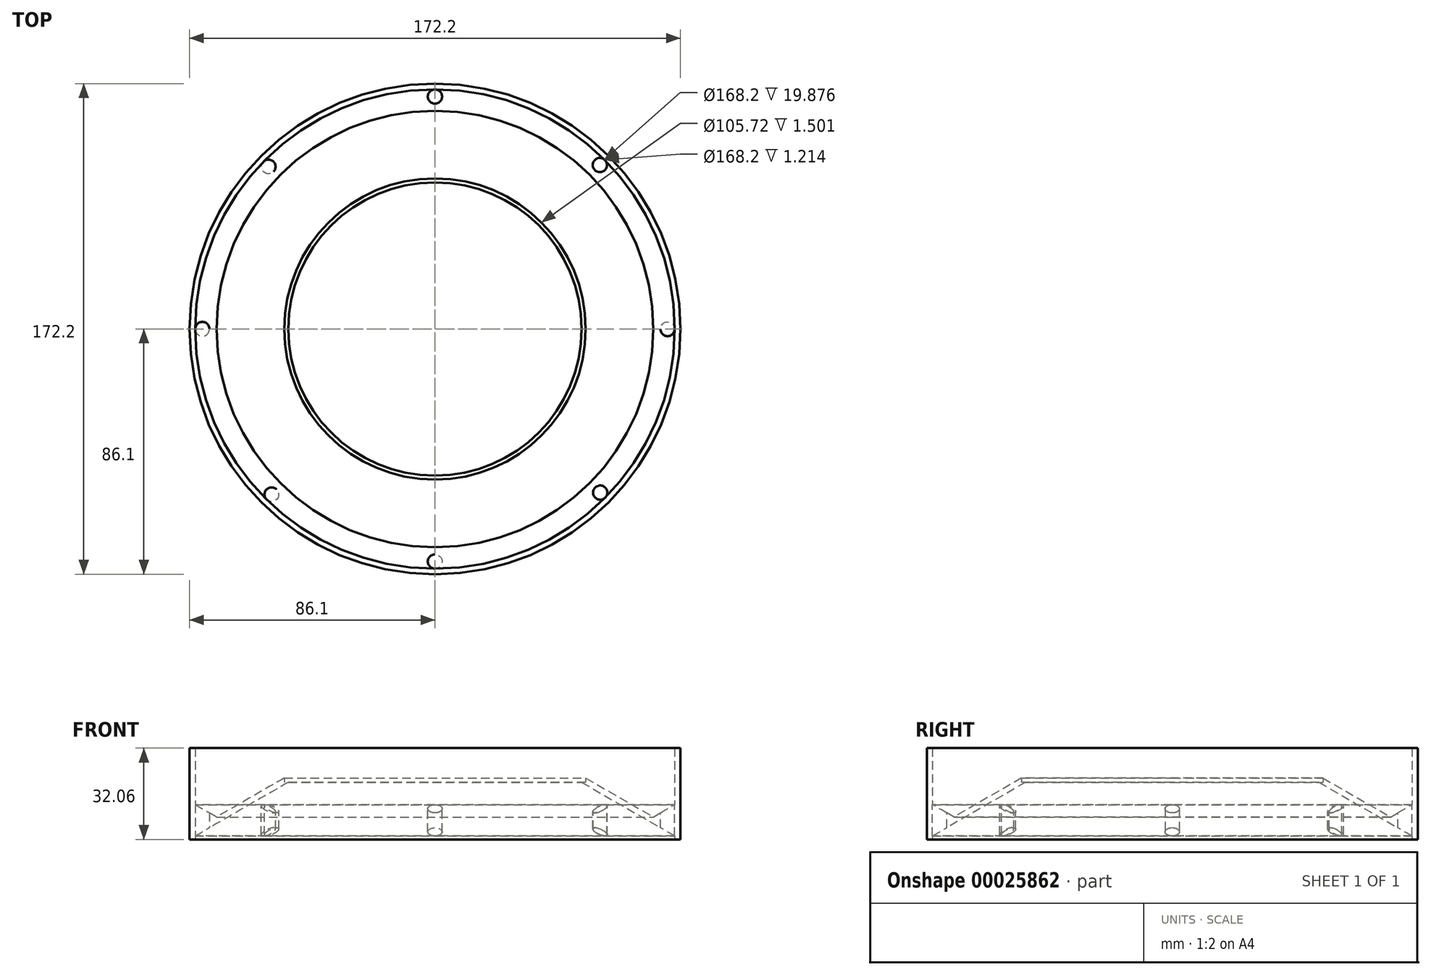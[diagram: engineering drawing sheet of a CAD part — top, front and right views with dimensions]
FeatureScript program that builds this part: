
annotation { "Feature Type Name" : "Feature", "Feature Type Description" : "" }
export const myFeature = defineFeature(function(context is Context, id is Id, definition is map)
    precondition{}
    {
        {
            var Q0;
            Q0=qCreatedBy(makeId("Top.planeOp"),FACE);
            var sketch = newSketch(context, id + "F0", { "sketchPlane" : qUnion([Q0])});
            skCircle(sketch, "E0", {"center": v(0, 0) * mm, "radius": 52.86 * mm});
            skSolve(sketch);
        }
        {
            var Q0;
            Q0=qCreatedBy(makeId("Front.planeOp"),FACE);
            var sketch = newSketch(context, id + "F1", { "sketchPlane" : qUnion([Q0])});
            skLineSegment(sketch, "E1", {"start": v(0, -28.34) * mm, "end": v(0, 33.36) * mm});
            skSolve(sketch);
        }
        {
            var Q0;
            Q0=qCreatedBy(makeId("Front.planeOp"),FACE);
            var sketch = newSketch(context, id + "F2", { "sketchPlane" : qUnion([Q0])});
            skLineSegment(sketch, "E2", {"start": v(0, 0) * mm, "end": v(-51.46, 0) * mm});
            skLineSegment(sketch, "E3", {"start": v(-51.46, 0) * mm, "end": v(-86.1, -20) * mm});
            skLineSegment(sketch, "E4", {"start": v(-86.1, -20) * mm, "end": v(-86.1, 12) * mm});
            skLineSegment(sketch, "E5", {"start": v(-86.1, 12) * mm, "end": v(-84.1, 12) * mm});
            skLineSegment(sketch, "E6", {"start": v(-84.1, 12) * mm, "end": v(-84.1, -16.54) * mm});
            skLineSegment(sketch, "E7", {"start": v(-84.1, -16.54) * mm, "end": v(-52, 2) * mm});
            skLineSegment(sketch, "E8", {"start": v(-52, 2) * mm, "end": v(0, 2) * mm});
            skLineSegment(sketch, "E9", {"start": v(0, 2) * mm, "end": v(0, 0) * mm});
            skSolve(sketch);
        }
        {
            var Q0;
            Q0 = qSketchRegion(id + "F2", true);
            var Q1;
            Q1=sQuery(id+"F1.wireOp",EDGE,"E1");
            revolve(context, id + "F3", {"entities" : qUnion([Q0]), "axis" : qUnion([Q1]), "revolveType" : RevolveType.FULL});
        }
        {
            var Q0;
            Q0 = qSketchRegion(id + "F0", true);
            extrude(context, id + "F4", {"entities" : qUnion([Q0]), "operationType" : NewBodyOperationType.REMOVE, "depth" : 9.85 * mm});
        }
        {
            var Q0;
            Q0=qCreatedBy(makeId("Top.planeOp"),FACE);
            var sketch = newSketch(context, id + "F5", { "sketchPlane" : qUnion([Q0])});
            skCircle(sketch, "E10", {"center": v(-81.6, 0) * mm, "radius": 2.5 * mm});
            skCircle(sketch, "E11", {"center": v(0, 0) * mm, "radius": 2.5 * mm});
            skSolve(sketch);
        }
        {
            var Q0;
            Q0 = qSketchRegion(id + "F5", true);
            extrude(context, id + "F6", {"entities" : qUnion([Q0]), "operationType" : NewBodyOperationType.REMOVE, "depth" : 25 * mm, "hasSecondDirection" : true, "secondDirectionOppositeDirection" : true, "secondDirectionDepth" : 25 * mm});
        }
        {
            var Q0;
            Q0=qCreatedBy(makeId("Top.planeOp"),FACE);
            var sketch = newSketch(context, id + "F7", { "sketchPlane" : qUnion([Q0])});
            skCircle(sketch, "E12", {"center": v(-58.42, 56.97) * mm, "radius": 2.5 * mm});
            skCircle(sketch, "E13", {"center": v(0, 81.6) * mm, "radius": 2.5 * mm});
            skCircle(sketch, "E14", {"center": v(57.85, 57.55) * mm, "radius": 2.5 * mm});
            skCircle(sketch, "E15", {"center": v(81.6, 0) * mm, "radius": 2.5 * mm});
            skCircle(sketch, "E16", {"center": v(57.97, -57.43) * mm, "radius": 2.5 * mm});
            skCircle(sketch, "E17", {"center": v(0, -81.6) * mm, "radius": 2.5 * mm});
            skCircle(sketch, "E18", {"center": v(-57.31, -58.09) * mm, "radius": 2.5 * mm});
            skSolve(sketch);
        }
        {
            var Q0;
            Q0 = qSketchRegion(id + "F7", true);
            extrude(context, id + "F8", {"entities" : qUnion([Q0]), "operationType" : NewBodyOperationType.REMOVE, "oppositeDirection" : true, "depth" : 25 * mm, "hasSecondDirection" : true, "secondDirectionOppositeDirection" : false, "secondDirectionDepth" : 25 * mm});
        }
        {
            var Q0;
            Q0=qCreatedBy(makeId("Front.planeOp"),FACE);
            var sketch = newSketch(context, id + "F9", { "sketchPlane" : qUnion([Q0])});
            skLineSegment(sketch, "E19.bottom", {"start": v(-86.1, -20.06) * mm, "end": v(-84.1, -20.06) * mm});
            skLineSegment(sketch, "E19.top", {"start": v(-86.1, -16.32) * mm, "end": v(-84.1, -16.32) * mm});
            skLineSegment(sketch, "E19.left", {"start": v(-86.1, -20.06) * mm, "end": v(-86.1, -16.32) * mm});
            skLineSegment(sketch, "E19.right", {"start": v(-84.1, -20.06) * mm, "end": v(-84.1, -16.32) * mm});
            skSolve(sketch);
        }
        {
            var Q0;
            Q0 = qSketchRegion(id + "F9", true);
            var Q1;
            Q1=sQuery(id+"F1.wireOp",EDGE,"E1");
            revolve(context, id + "F10", {"operationType" : NewBodyOperationType.ADD, "entities" : qUnion([Q0]), "axis" : qUnion([Q1]), "revolveType" : RevolveType.FULL});
        }
        {
            var Q0;
            {var subQ0=sQuery(id+"F2.wireOp",EDGE,"E6");var subQ1=sQuery(id+"F2.wireOp",EDGE,"E7");Q0=makeQuery(id+"F8.boolean.opBoolean","SPLIT",EDGE,{"disambiguationData":[TD([makeQuery(id+"F3.opRevolve","SWEPT_FACE",FACE,{"disambiguationData":[OSD([subQ0])]}),makeQuery(id+"F3.opRevolve","SWEPT_FACE",FACE,{"disambiguationData":[OSD([subQ1])]}),makeQuery(id+"F6.boolean.opBoolean","COPY",FACE,{"derivedFrom":makeQuery(id+"F6.opExtrude","SWEPT_FACE",FACE,{"disambiguationData":[OSD([sQuery(id+"F5.wireOp",EDGE,"E10")])]})}),makeQuery(id+"F8.opExtrude","SWEPT_FACE",FACE,{"disambiguationData":[OSD([sQuery(id+"F7.wireOp",EDGE,"E12")])]})])],"derivedFrom":makeQuery(id+"F3.opRevolve","SWEPT_EDGE",EDGE,{"disambiguationData":[OSD([subQ0,subQ1])]})});}
            var Q1;
            {var subQ0=sQuery(id+"F2.wireOp",EDGE,"E6");var subQ1=sQuery(id+"F2.wireOp",EDGE,"E7");Q1=makeQuery(id+"F8.boolean.opBoolean","SPLIT",EDGE,{"disambiguationData":[TD([makeQuery(id+"F3.opRevolve","SWEPT_FACE",FACE,{"disambiguationData":[OSD([subQ0])]}),makeQuery(id+"F3.opRevolve","SWEPT_FACE",FACE,{"disambiguationData":[OSD([subQ1])]}),makeQuery(id+"F8.opExtrude","SWEPT_FACE",FACE,{"disambiguationData":[OSD([sQuery(id+"F7.wireOp",EDGE,"E12")])]}),makeQuery(id+"F8.opExtrude","SWEPT_FACE",FACE,{"disambiguationData":[OSD([sQuery(id+"F7.wireOp",EDGE,"E13")])]})])],"derivedFrom":makeQuery(id+"F3.opRevolve","SWEPT_EDGE",EDGE,{"disambiguationData":[OSD([subQ0,subQ1])]})});}
            var Q2;
            {var subQ0=sQuery(id+"F2.wireOp",EDGE,"E6");var subQ1=sQuery(id+"F2.wireOp",EDGE,"E7");Q2=makeQuery(id+"F8.boolean.opBoolean","SPLIT",EDGE,{"disambiguationData":[TD([makeQuery(id+"F3.opRevolve","SWEPT_FACE",FACE,{"disambiguationData":[OSD([subQ0])]}),makeQuery(id+"F3.opRevolve","SWEPT_FACE",FACE,{"disambiguationData":[OSD([subQ1])]}),makeQuery(id+"F6.boolean.opBoolean","COPY",FACE,{"derivedFrom":makeQuery(id+"F6.opExtrude","SWEPT_FACE",FACE,{"disambiguationData":[OSD([sQuery(id+"F5.wireOp",EDGE,"E10")])]})}),makeQuery(id+"F8.opExtrude","SWEPT_FACE",FACE,{"disambiguationData":[OSD([sQuery(id+"F7.wireOp",EDGE,"E18")])]})])],"derivedFrom":makeQuery(id+"F3.opRevolve","SWEPT_EDGE",EDGE,{"disambiguationData":[OSD([subQ0,subQ1])]})});}
            var Q3;
            {var subQ0=sQuery(id+"F2.wireOp",EDGE,"E6");var subQ1=sQuery(id+"F2.wireOp",EDGE,"E7");Q3=makeQuery(id+"F8.boolean.opBoolean","SPLIT",EDGE,{"disambiguationData":[TD([makeQuery(id+"F3.opRevolve","SWEPT_FACE",FACE,{"disambiguationData":[OSD([subQ0])]}),makeQuery(id+"F3.opRevolve","SWEPT_FACE",FACE,{"disambiguationData":[OSD([subQ1])]}),makeQuery(id+"F8.opExtrude","SWEPT_FACE",FACE,{"disambiguationData":[OSD([sQuery(id+"F7.wireOp",EDGE,"E17")])]}),makeQuery(id+"F8.opExtrude","SWEPT_FACE",FACE,{"disambiguationData":[OSD([sQuery(id+"F7.wireOp",EDGE,"E18")])]})])],"derivedFrom":makeQuery(id+"F3.opRevolve","SWEPT_EDGE",EDGE,{"disambiguationData":[OSD([subQ0,subQ1])]})});}
            var Q4;
            {var subQ0=sQuery(id+"F2.wireOp",EDGE,"E6");var subQ1=sQuery(id+"F2.wireOp",EDGE,"E7");Q4=makeQuery(id+"F8.boolean.opBoolean","SPLIT",EDGE,{"disambiguationData":[TD([makeQuery(id+"F3.opRevolve","SWEPT_FACE",FACE,{"disambiguationData":[OSD([subQ0])]}),makeQuery(id+"F3.opRevolve","SWEPT_FACE",FACE,{"disambiguationData":[OSD([subQ1])]}),makeQuery(id+"F8.opExtrude","SWEPT_FACE",FACE,{"disambiguationData":[OSD([sQuery(id+"F7.wireOp",EDGE,"E16")])]}),makeQuery(id+"F8.opExtrude","SWEPT_FACE",FACE,{"disambiguationData":[OSD([sQuery(id+"F7.wireOp",EDGE,"E17")])]})])],"derivedFrom":makeQuery(id+"F3.opRevolve","SWEPT_EDGE",EDGE,{"disambiguationData":[OSD([subQ0,subQ1])]})});}
            var Q5;
            {var subQ0=sQuery(id+"F2.wireOp",EDGE,"E6");var subQ1=sQuery(id+"F2.wireOp",EDGE,"E7");Q5=makeQuery(id+"F8.boolean.opBoolean","SPLIT",EDGE,{"disambiguationData":[TD([makeQuery(id+"F3.opRevolve","SWEPT_FACE",FACE,{"disambiguationData":[OSD([subQ0])]}),makeQuery(id+"F3.opRevolve","SWEPT_FACE",FACE,{"disambiguationData":[OSD([subQ1])]}),makeQuery(id+"F8.opExtrude","SWEPT_FACE",FACE,{"disambiguationData":[OSD([sQuery(id+"F7.wireOp",EDGE,"E15")])]}),makeQuery(id+"F8.opExtrude","SWEPT_FACE",FACE,{"disambiguationData":[OSD([sQuery(id+"F7.wireOp",EDGE,"E16")])]})])],"derivedFrom":makeQuery(id+"F3.opRevolve","SWEPT_EDGE",EDGE,{"disambiguationData":[OSD([subQ0,subQ1])]})});}
            var Q6;
            {var subQ0=sQuery(id+"F2.wireOp",EDGE,"E6");var subQ1=sQuery(id+"F2.wireOp",EDGE,"E7");Q6=makeQuery(id+"F8.boolean.opBoolean","SPLIT",EDGE,{"disambiguationData":[TD([makeQuery(id+"F3.opRevolve","SWEPT_FACE",FACE,{"disambiguationData":[OSD([subQ0])]}),makeQuery(id+"F3.opRevolve","SWEPT_FACE",FACE,{"disambiguationData":[OSD([subQ1])]}),makeQuery(id+"F8.opExtrude","SWEPT_FACE",FACE,{"disambiguationData":[OSD([sQuery(id+"F7.wireOp",EDGE,"E13")])]}),makeQuery(id+"F8.opExtrude","SWEPT_FACE",FACE,{"disambiguationData":[OSD([sQuery(id+"F7.wireOp",EDGE,"E14")])]})])],"derivedFrom":makeQuery(id+"F3.opRevolve","SWEPT_EDGE",EDGE,{"disambiguationData":[OSD([subQ0,subQ1])]})});}
            var Q7;
            {var subQ0=sQuery(id+"F2.wireOp",EDGE,"E6");var subQ1=sQuery(id+"F2.wireOp",EDGE,"E7");Q7=makeQuery(id+"F8.boolean.opBoolean","SPLIT",EDGE,{"disambiguationData":[TD([makeQuery(id+"F3.opRevolve","SWEPT_FACE",FACE,{"disambiguationData":[OSD([subQ0])]}),makeQuery(id+"F3.opRevolve","SWEPT_FACE",FACE,{"disambiguationData":[OSD([subQ1])]}),makeQuery(id+"F8.opExtrude","SWEPT_FACE",FACE,{"disambiguationData":[OSD([sQuery(id+"F7.wireOp",EDGE,"E14")])]}),makeQuery(id+"F8.opExtrude","SWEPT_FACE",FACE,{"disambiguationData":[OSD([sQuery(id+"F7.wireOp",EDGE,"E15")])]})])],"derivedFrom":makeQuery(id+"F3.opRevolve","SWEPT_EDGE",EDGE,{"disambiguationData":[OSD([subQ0,subQ1])]})});}
            chamfer(context, id + "F11", {"entities" : qUnion([Q0, Q1, Q2, Q3, Q4, Q5, Q6, Q7]), "width" : 5 * mm, "tangentPropagation" : true});
        }
    });
